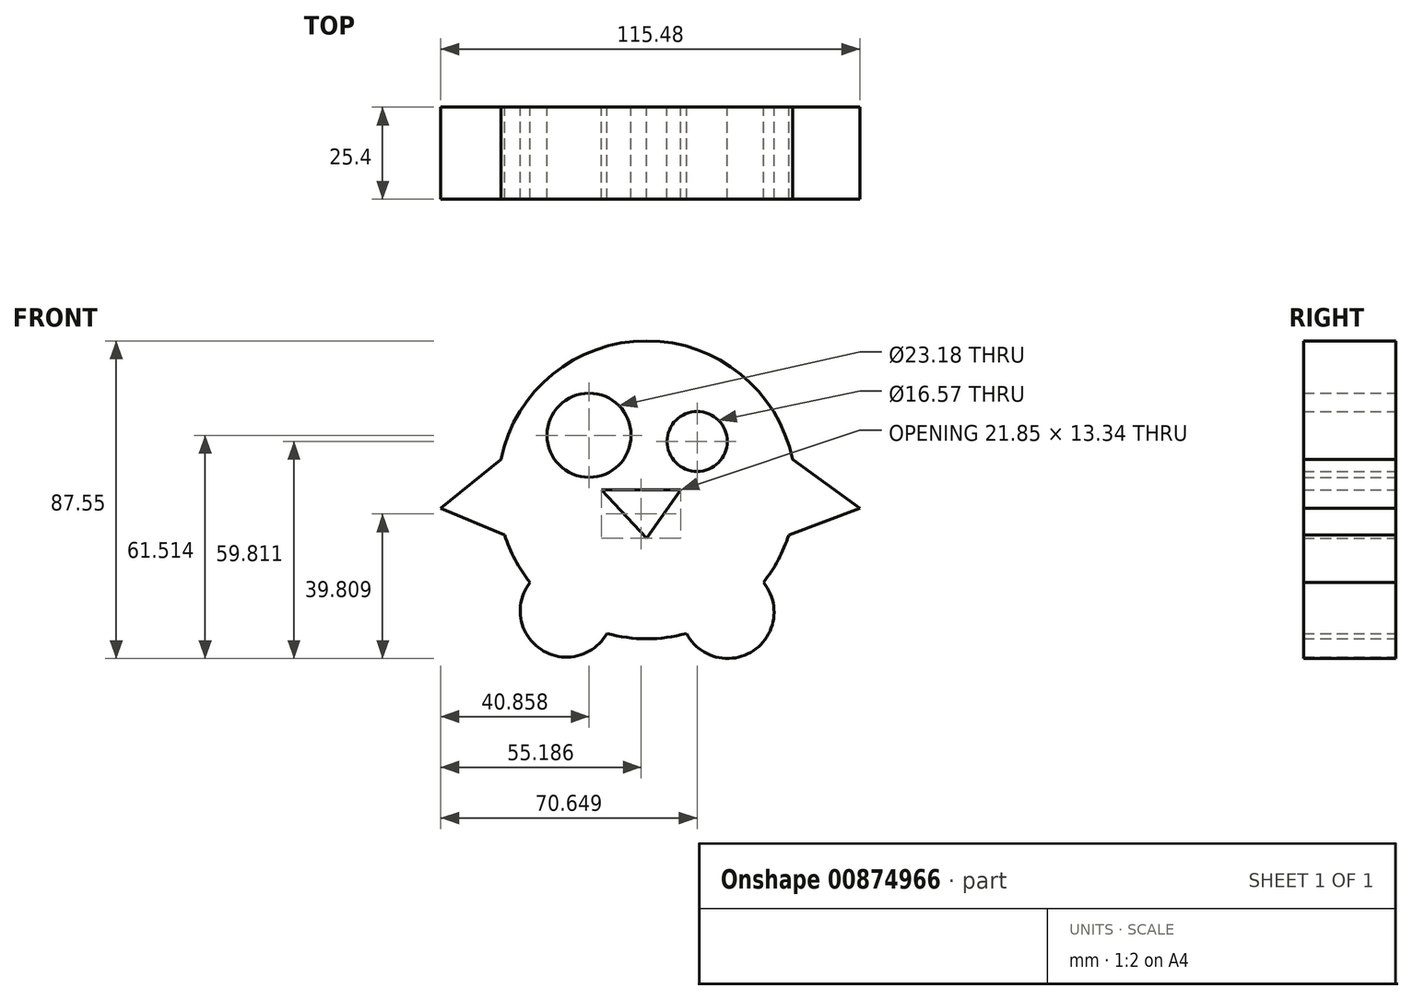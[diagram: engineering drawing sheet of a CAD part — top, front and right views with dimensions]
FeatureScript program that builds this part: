
annotation { "Feature Type Name" : "Feature", "Feature Type Description" : "" }
export const myFeature = defineFeature(function(context is Context, id is Id, definition is map)
    precondition{}
    {
        {
            var Q0;
            Q0=qCreatedBy(makeId("Front.planeOp"),FACE);
            var sketch = newSketch(context, id + "F0", { "sketchPlane" : qUnion([Q0])});
            skCircle(sketch, "E0", {"center": v(-20.85, 18.02) * mm, "radius": 41.08 * mm});
            skLineSegment(sketch, "E1", {"start": v(-61.06, 26.45) * mm, "end": v(-77.6, 12.9) * mm});
            skLineSegment(sketch, "E2", {"start": v(-77.6, 12.9) * mm, "end": v(-60.01, 5.6) * mm});
            skLineSegment(sketch, "E3", {"start": v(19.35, 26.45) * mm, "end": v(37.88, 12.9) * mm});
            skArc(sketch, "E4", {"start": v(-53.03, -7.52) * mm, "mid": v(-50, -25.98) * mm, "end": v(-31.82, -21.57) * mm});
            skArc(sketch, "E5", {"start": v(-9.88, -21.57) * mm, "mid": v(8.53, -26.33) * mm, "end": v(11.32, -7.52) * mm});
            skLineSegment(sketch, "E6", {"start": v(18.3, 5.6) * mm, "end": v(37.88, 12.9) * mm});
            skCircle(sketch, "E7", {"center": v(-36.74, 33.05) * mm, "radius": 11.6 * mm});
            skCircle(sketch, "E8", {"center": v(-6.95, 31.35) * mm, "radius": 8.29 * mm});
            skArc(sketch, "E9", {"start": v(1.47, -15.67) * mm, "mid": v(-20.65, -2.9) * mm, "end": v(-42.96, -15.35) * mm});
            skLineSegment(sketch, "E10", {"start": v(-20.85, 18.02) * mm, "end": v(-33.34, 18.02) * mm});
            skLineSegment(sketch, "E11", {"start": v(-33.34, 18.02) * mm, "end": v(-20.85, 18.02) * mm});
            skLineSegment(sketch, "E12", {"start": v(-11.5, 18.02) * mm, "end": v(-20.85, 4.68) * mm});
            skLineSegment(sketch, "E13", {"start": v(-20.85, 4.68) * mm, "end": v(-33.34, 18.02) * mm});
            skLineSegment(sketch, "E14", {"start": v(-20.85, 18.02) * mm, "end": v(-11.5, 18.02) * mm});
            skSolve(sketch);
        }
        {
            var Q0;
            Q0 = qSketchRegion(id + "F0", true);
            extrude(context, id + "F1", {"entities" : qUnion([Q0]), "depth" : 25.4 * mm, "offsetDistance" : 25.4 * mm});
        }
    });
